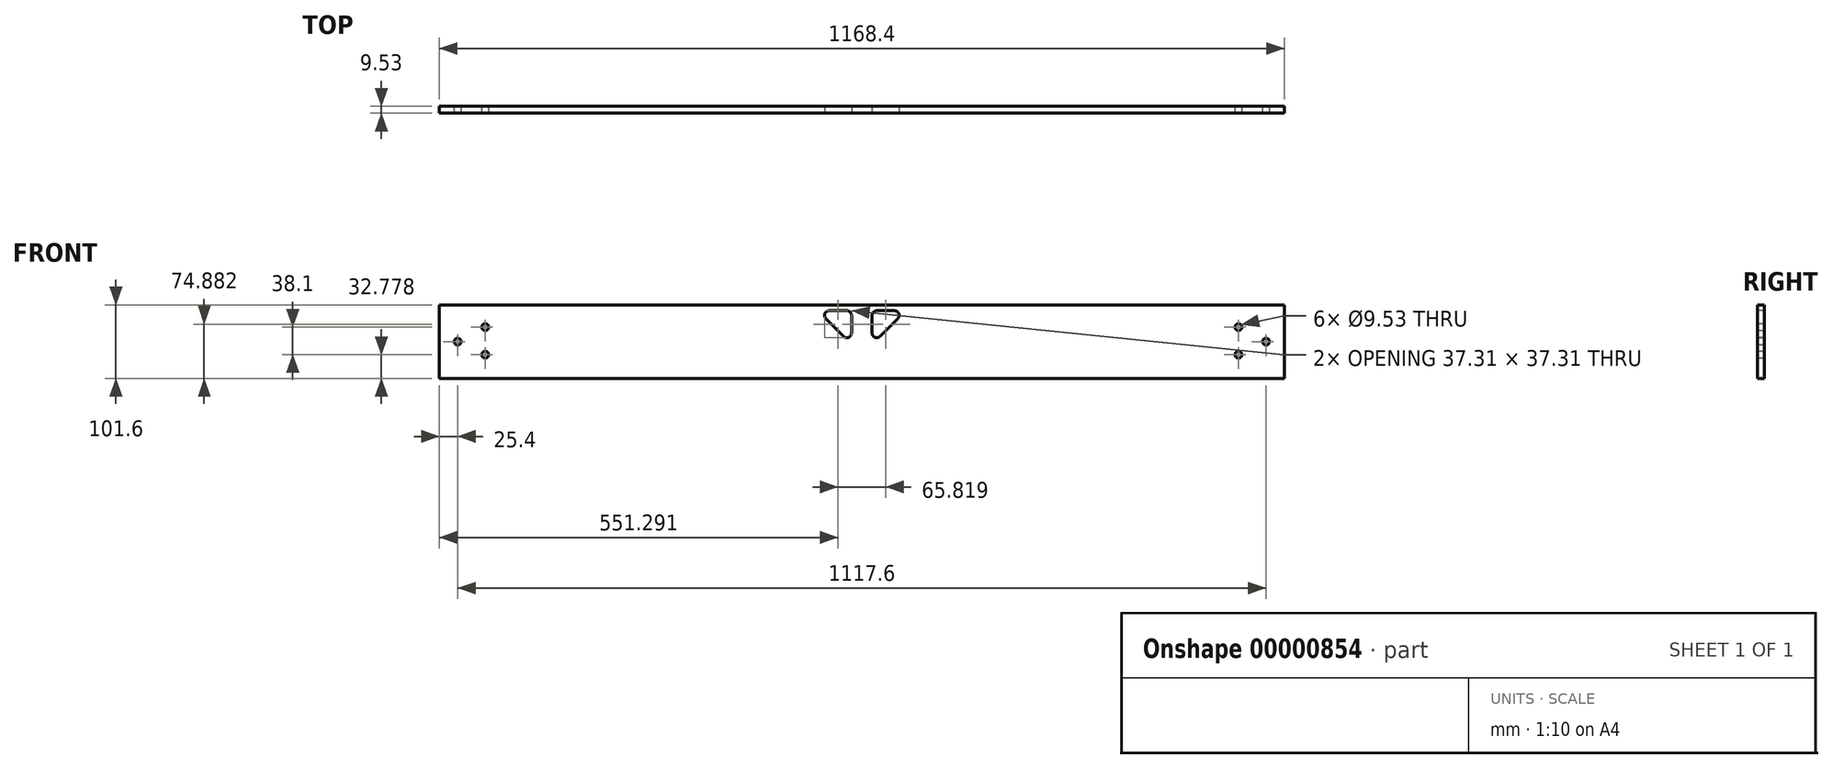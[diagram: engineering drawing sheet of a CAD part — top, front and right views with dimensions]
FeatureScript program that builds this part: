
annotation { "Feature Type Name" : "Feature", "Feature Type Description" : "" }
export const myFeature = defineFeature(function(context is Context, id is Id, definition is map)
    precondition{}
    {
        {
            var Q0;
            Q0=qCreatedBy(makeId("Front.planeOp"),FACE);
            var sketch = newSketch(context, id + "F0", { "sketchPlane" : qUnion([Q0])});
            skLineSegment(sketch, "E0.bottom", {"start": v(-584.2, 50.8) * mm, "end": v(0, 50.8) * mm});
            skLineSegment(sketch, "E0.top", {"start": v(-584.2, -50.8) * mm, "end": v(0, -50.8) * mm});
            skLineSegment(sketch, "E0.left", {"start": v(-584.2, 50.8) * mm, "end": v(-584.2, -50.8) * mm});
            skLineSegment(sketch, "E0.right", {"start": v(0, 50.8) * mm, "end": v(0, -50.8) * mm});
            skLineSegment(sketch, "E1", {"start": v(0, 177.85) * mm, "end": v(0, -210.72) * mm, "construction": true});
            skLineSegment(sketch, "E2", {"start": v(-653.63, 0) * mm, "end": v(548.06, 0) * mm, "construction": true});
            skLineSegment(sketch, "E3", {"start": v(-14.25, 36.39) * mm, "end": v(-14.25, 11.75) * mm});
            skLineSegment(sketch, "E4", {"start": v(-25.1, 7.26) * mm, "end": v(-49.73, 31.9) * mm});
            skLineSegment(sketch, "E5", {"start": v(-45.24, 42.74) * mm, "end": v(-20.6, 42.74) * mm});
            skPoint(sketch, "E6.visualSharp", {"position": v(-60.57, 42.74) * mm});
            skArc(sketch, "E6.filletArc", {"start": v(-45.24, 42.74) * mm, "mid": v(-51.11, 38.82) * mm, "end": v(-49.73, 31.9) * mm});
            skPoint(sketch, "E7.visualSharp", {"position": v(-14.25, -3.58) * mm});
            skArc(sketch, "E7.filletArc", {"start": v(-25.1, 7.26) * mm, "mid": v(-18.17, 5.88) * mm, "end": v(-14.25, 11.75) * mm});
            skPoint(sketch, "E8.visualSharp", {"position": v(-14.25, 42.74) * mm});
            skArc(sketch, "E8.filletArc", {"start": v(-14.25, 36.39) * mm, "mid": v(-16.11, 40.88) * mm, "end": v(-20.6, 42.74) * mm});
            skCircle(sketch, "E9", {"center": v(-520.7, 20.08) * mm, "radius": 4.76 * mm});
            skCircle(sketch, "E10", {"center": v(-558.8, 0) * mm, "radius": 4.76 * mm});
            skCircle(sketch, "E11", {"center": v(-520.7, -18.02) * mm, "radius": 4.76 * mm});
            skLineSegment(sketch, "E12", {"start": v(-520.7, 92.21) * mm, "end": v(-520.7, -109.26) * mm, "construction": true});
            skSolve(sketch);
        }
        {
            var Q0;
            Q0=makeQuery(id+"F0.imprint","IMPRINT",FACE,{"disambiguationData":[TD([[makeQuery(id+"F0.imprint","IMPRINT",EDGE,{"derivedFrom":sQuery(id+"F0.wireOp",EDGE,"E0.bottom")}),-1.0]])]});
            extrude(context, id + "F1", {"entities" : qUnion([Q0]), "oppositeDirection" : true, "depth" : 9.52 * mm});
        }
        {
            var Q0;
            Q0=makeQuery(id+"F1.opExtrude","SWEPT_BODY",BODY,{"disambiguationData":[OSD([sQuery(id+"F0.wireOp",EDGE,"E0.bottom"),sQuery(id+"F0.wireOp",EDGE,"E0.top"),sQuery(id+"F0.wireOp",EDGE,"E0.left"),sQuery(id+"F0.wireOp",EDGE,"E0.right")])]});
            var Q1;
            Q1=makeQuery(id+"F1.opExtrude","SWEPT_FACE",FACE,{"disambiguationData":[OSD([sQuery(id+"F0.wireOp",EDGE,"E0.right")])]});
            mirror(context, id + "F2", {"operationType" : NewBodyOperationType.ADD, "entities" : qUnion([Q0]), "mirrorPlane" : qUnion([Q1])});
        }
    });
